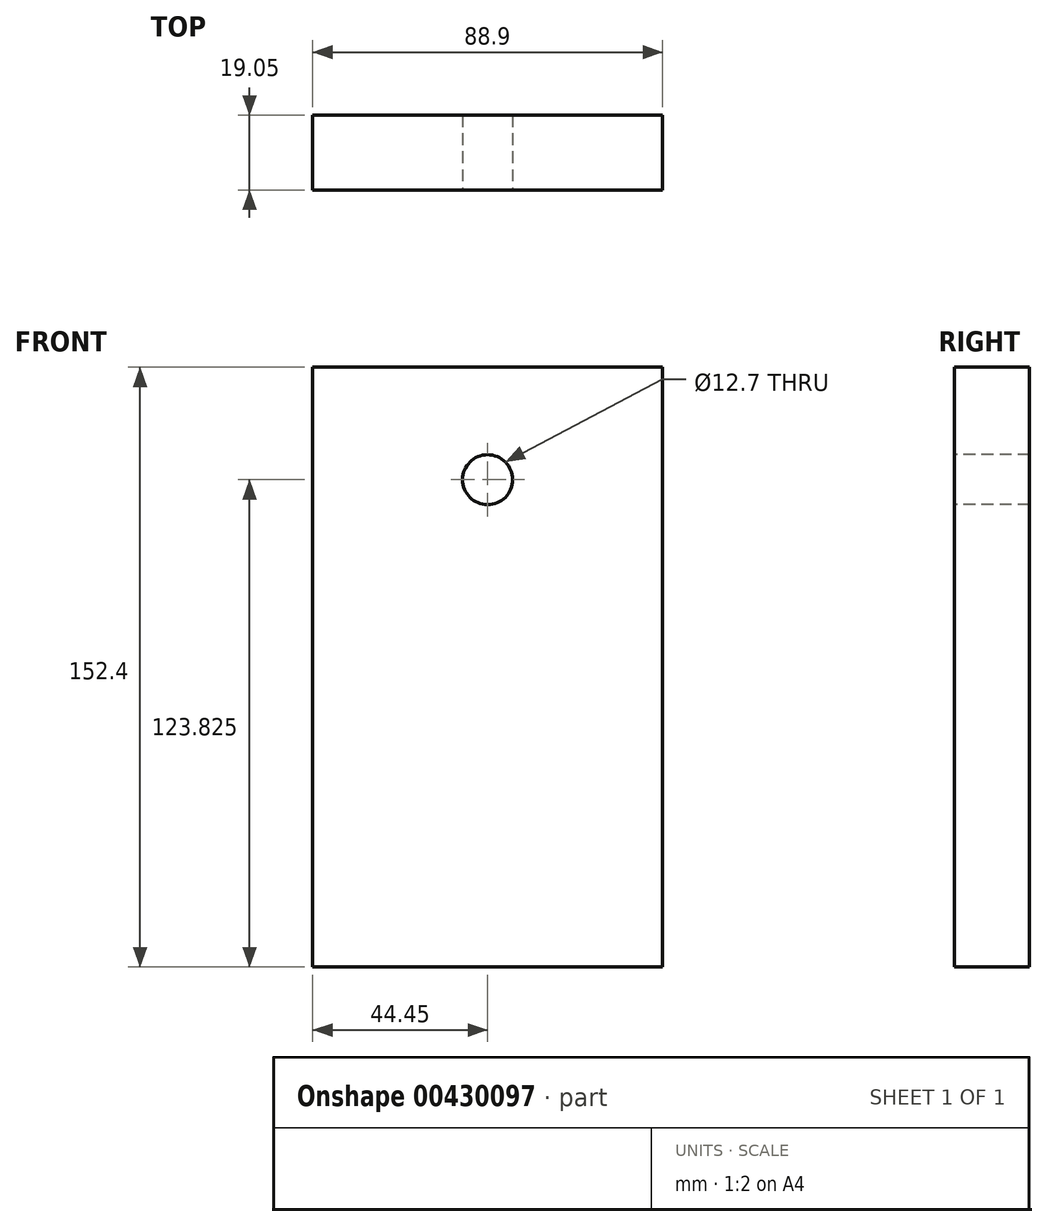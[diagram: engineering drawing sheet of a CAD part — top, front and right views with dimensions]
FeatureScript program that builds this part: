
annotation { "Feature Type Name" : "Feature", "Feature Type Description" : "" }
export const myFeature = defineFeature(function(context is Context, id is Id, definition is map)
    precondition{}
    {
        {
            var Q0;
            Q0=qCreatedBy(makeId("Top.planeOp"),FACE);
            var sketch = newSketch(context, id + "F0", { "sketchPlane" : qUnion([Q0])});
            skLineSegment(sketch, "E0.bottom", {"start": v(0, 0) * mm, "end": v(88.9, 0) * mm});
            skLineSegment(sketch, "E0.top", {"start": v(0, -19.05) * mm, "end": v(88.9, -19.05) * mm});
            skLineSegment(sketch, "E0.left", {"start": v(0, 0) * mm, "end": v(0, -19.05) * mm});
            skLineSegment(sketch, "E0.right", {"start": v(88.9, 0) * mm, "end": v(88.9, -19.05) * mm});
            skSolve(sketch);
        }
        {
            var Q0;
            Q0=makeQuery(id+"F0.imprint","IMPRINT",FACE,{"disambiguationData":[TD([[makeQuery(id+"F0.imprint","IMPRINT",EDGE,{"derivedFrom":sQuery(id+"F0.wireOp",EDGE,"E0.bottom")}),-1.0]])]});
            extrude(context, id + "F1", {"entities" : qUnion([Q0]), "depth" : 152.4 * mm});
        }
        {
            var Q0;
            Q0=makeQuery(id+"F1.opExtrude","SWEPT_FACE",FACE,{"disambiguationData":[OSD([sQuery(id+"F0.wireOp",EDGE,"E0.top")])]});
            var sketch = newSketch(context, id + "F2", { "sketchPlane" : qUnion([Q0])});
            skPoint(sketch, "E1", {"position": v(44.45, 123.83) * mm});
            skSolve(sketch);
        }
        {
            var Q0;
            Q0=sQuery(id+"F2.wireOp",VERTEX,"E1");
            var Q1;
            Q1=makeQuery(id+"F1.opExtrude","SWEPT_BODY",BODY,{"disambiguationData":[OSD([sQuery(id+"F0.wireOp",EDGE,"E0.bottom"),sQuery(id+"F0.wireOp",EDGE,"E0.top"),sQuery(id+"F0.wireOp",EDGE,"E0.left"),sQuery(id+"F0.wireOp",EDGE,"E0.right")])]});
            hole(context, id + "F3", {"style" : HoleStyle.SIMPLE, "endStyle" : HoleEndStyle.THROUGH, "holeDiameter" : 12.7 * mm, "isTappedThrough" : true, "tappedDepth" : 12.7 * mm, "tapClearance" : 3, "locations" : qUnion([Q0]), "scope" : qUnion([Q1])});
        }
    });
